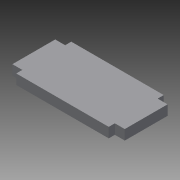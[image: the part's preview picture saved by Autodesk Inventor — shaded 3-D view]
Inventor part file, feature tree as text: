
AUTODESK INVENTOR PART (.ipt)
format: ipt  version: 2013 (Build 170138000, 138)  size: 97,792 bytes
history: native  units: mm
features: other x2, extrude x1, sketch x1
ambient origin geometry x8: Origin, YZ Plane, XZ Plane, XY Plane, X Axis, Y Axis, Z Axis, Center Point
feature tree (4):
  other  "Blocks"
  extrude  "Extrusion5"  Depth=3.0mm
  sketch  "Sketch1"  dims[d0=3.0mm d2=3.0mm d3=0.1mm d7=22.5mm d8=12.4mm d9=4.5mm d10=4.5mm d11=2.0mm d12=2.0mm d38=30.25mm d39=18.0mm d40=3.25mm d41=14.0mm d42=3.25mm d43=0.0mm]
  other  "Block1"
